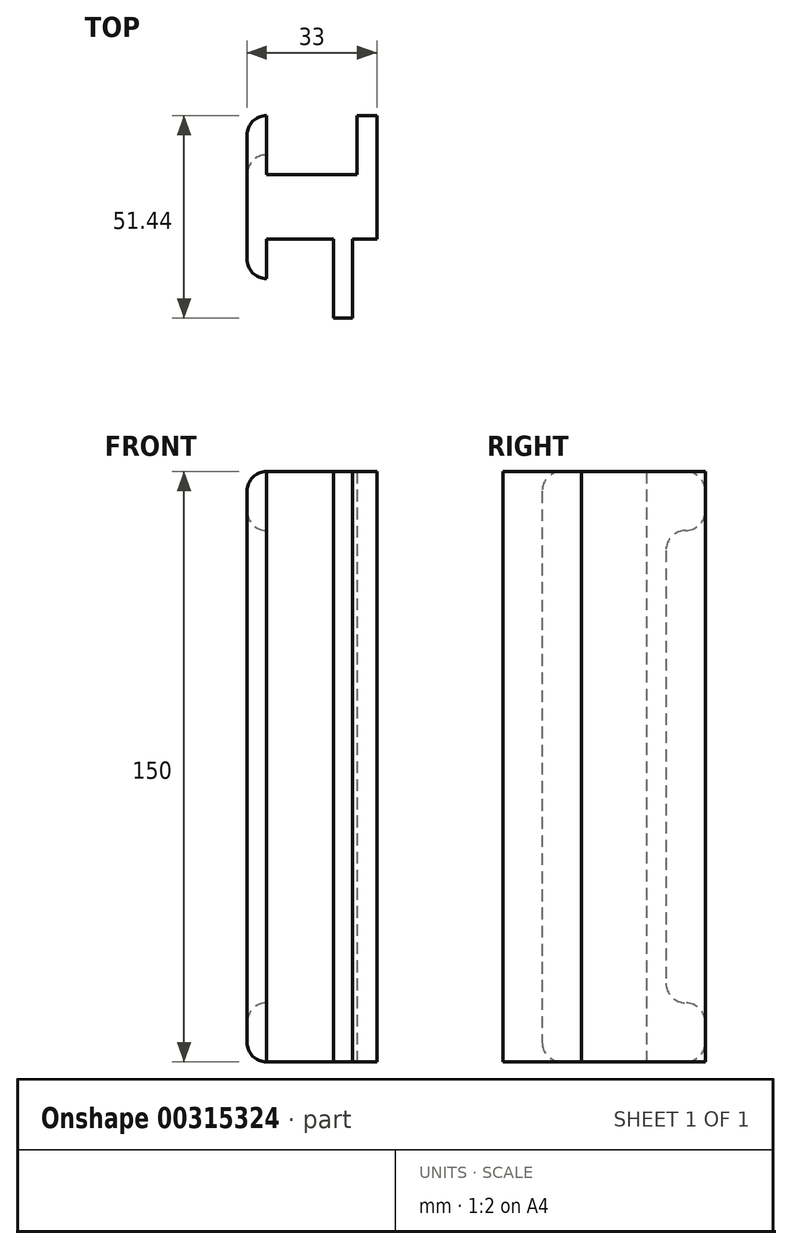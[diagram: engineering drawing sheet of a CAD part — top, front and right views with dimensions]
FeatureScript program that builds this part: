
annotation { "Feature Type Name" : "Feature", "Feature Type Description" : "" }
export const myFeature = defineFeature(function(context is Context, id is Id, definition is map)
    precondition{}
    {
        {
            var Q0;
            Q0=qCreatedBy(makeId("Top.planeOp"),FACE);
            var sketch = newSketch(context, id + "F0", { "sketchPlane" : qUnion([Q0])});
            skLineSegment(sketch, "E0", {"start": v(-22, 31.44) * mm, "end": v(-17, 31.44) * mm});
            skLineSegment(sketch, "E1", {"start": v(-17, 31.44) * mm, "end": v(-17, 16.44) * mm});
            skLineSegment(sketch, "E2", {"start": v(-17, 16.44) * mm, "end": v(6, 16.44) * mm});
            skLineSegment(sketch, "E3", {"start": v(6, 16.44) * mm, "end": v(6, 31.44) * mm});
            skLineSegment(sketch, "E4", {"start": v(6, 31.44) * mm, "end": v(11, 31.44) * mm});
            skLineSegment(sketch, "E5", {"start": v(11, 31.44) * mm, "end": v(11, 0) * mm});
            skLineSegment(sketch, "E6", {"start": v(11, 0) * mm, "end": v(4.8, 0) * mm});
            skLineSegment(sketch, "E7", {"start": v(4.8, 0) * mm, "end": v(4.8, -20) * mm});
            skLineSegment(sketch, "E8", {"start": v(4.8, -20) * mm, "end": v(0, -20) * mm});
            skLineSegment(sketch, "E9", {"start": v(0, -20) * mm, "end": v(0, 0) * mm});
            skLineSegment(sketch, "E10", {"start": v(0, 0) * mm, "end": v(-17, 0) * mm});
            skLineSegment(sketch, "E11", {"start": v(-17, 0) * mm, "end": v(-17, -10) * mm});
            skLineSegment(sketch, "E12", {"start": v(-17, -10) * mm, "end": v(-22, -10) * mm});
            skLineSegment(sketch, "E13", {"start": v(-22, -10) * mm, "end": v(-22, 31.44) * mm});
            skSolve(sketch);
        }
        {
            var Q0;
            Q0=makeQuery(id+"F0.imprint","IMPRINT",FACE,{"disambiguationData":[TD([[makeQuery(id+"F0.imprint","IMPRINT",EDGE,{"derivedFrom":sQuery(id+"F0.wireOp",EDGE,"E0")}),-1.0]])]});
            extrude(context, id + "F1", {"entities" : qUnion([Q0]), "depth" : 150 * mm});
        }
        {
            var Q0;
            Q0=qCreatedBy(makeId("Right.planeOp"),FACE);
            var sketch = newSketch(context, id + "F2", { "sketchPlane" : qUnion([Q0])});
            skLineSegment(sketch, "E14.bottom", {"start": v(56.03, 135) * mm, "end": v(21.44, 135) * mm});
            skLineSegment(sketch, "E14.top", {"start": v(56.03, 15) * mm, "end": v(21.44, 15) * mm});
            skLineSegment(sketch, "E14.left", {"start": v(56.03, 135) * mm, "end": v(56.03, 15) * mm});
            skLineSegment(sketch, "E14.right", {"start": v(21.44, 135) * mm, "end": v(21.44, 15) * mm});
            skSolve(sketch);
        }
        {
            var Q0;
            Q0 = qSketchRegion(id + "F2", true);
            extrude(context, id + "F3", {"entities" : qUnion([Q0]), "operationType" : NewBodyOperationType.REMOVE, "oppositeDirection" : true, "depth" : 25 * mm});
        }
        {
            var Q0;
            Q0=makeQuery(id+"F3.boolean.opBoolean","COPY",EDGE,{"derivedFrom":makeQuery(id+"F3.opExtrude","SWEPT_EDGE",EDGE,{"disambiguationData":[OSD([sQuery(id+"F2.wireOp",EDGE,"E14.bottom"),sQuery(id+"F2.wireOp",EDGE,"E14.right")])]})});
            var Q1;
            Q1=makeQuery(id+"F3.boolean.opBoolean","INTERSECT",EDGE,{"derivedFrom":[makeQuery(id+"F1.opExtrude","SWEPT_FACE",FACE,{"disambiguationData":[OSD([sQuery(id+"F0.wireOp",EDGE,"E0")])]}),makeQuery(id+"F3.opExtrude","SWEPT_FACE",FACE,{"disambiguationData":[OSD([sQuery(id+"F2.wireOp",EDGE,"E14.bottom")])]})]});
            var Q2;
            Q2=makeQuery(id+"F3.boolean.opBoolean","COPY",EDGE,{"derivedFrom":makeQuery(id+"F3.opExtrude","SWEPT_EDGE",EDGE,{"disambiguationData":[OSD([sQuery(id+"F2.wireOp",EDGE,"E14.top"),sQuery(id+"F2.wireOp",EDGE,"E14.right")])]})});
            var Q3;
            Q3=makeQuery(id+"F3.boolean.opBoolean","INTERSECT",EDGE,{"derivedFrom":[makeQuery(id+"F1.opExtrude","SWEPT_FACE",FACE,{"disambiguationData":[OSD([sQuery(id+"F0.wireOp",EDGE,"E0")])]}),makeQuery(id+"F3.opExtrude","SWEPT_FACE",FACE,{"disambiguationData":[OSD([sQuery(id+"F2.wireOp",EDGE,"E14.top")])]})]});
            var Q4;
            Q4=makeQuery(id+"F1.opExtrude","CAP_EDGE",EDGE,{"disambiguationData":[OSD([sQuery(id+"F0.wireOp",EDGE,"E0")])],"isStart":false});
            var Q5;
            Q5=makeQuery(id+"F1.opExtrude","CAP_EDGE",EDGE,{"disambiguationData":[OSD([sQuery(id+"F0.wireOp",EDGE,"E12")])],"isStart":false});
            var Q6;
            Q6=makeQuery(id+"F1.opExtrude","CAP_EDGE",EDGE,{"disambiguationData":[OSD([sQuery(id+"F0.wireOp",EDGE,"E0")])],"isStart":true});
            var Q7;
            Q7=makeQuery(id+"F1.opExtrude","CAP_EDGE",EDGE,{"disambiguationData":[OSD([sQuery(id+"F0.wireOp",EDGE,"E12")])],"isStart":true});
            var Q8;
            Q8=makeQuery(id+"F1.opExtrude","SWEPT_FACE",FACE,{"disambiguationData":[OSD([sQuery(id+"F0.wireOp",EDGE,"E13")])]});
            fillet(context, id + "F4", {"entities" : qUnion([Q0, Q1, Q2, Q3, Q4, Q5, Q6, Q7, Q8]), "radius" : 5 * mm, "tangentPropagation" : true, "allowEdgeOverflow" : false});
        }
    });
